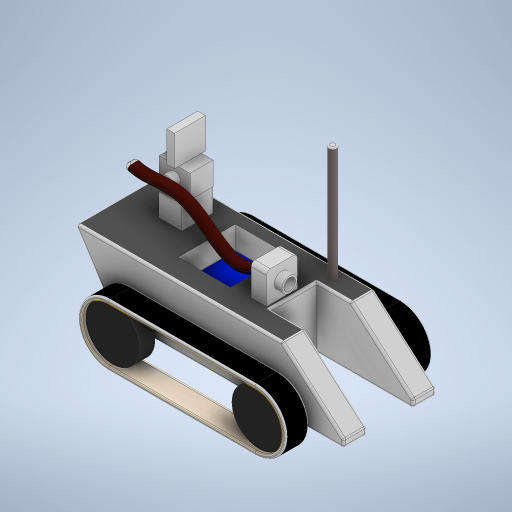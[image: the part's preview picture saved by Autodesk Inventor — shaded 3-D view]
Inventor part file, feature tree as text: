
AUTODESK INVENTOR PART (.ipt)
format: ipt  version: 2023.1 (Build 271208000, 208)  size: 786,944 bytes
history: native  units: in
note: dims shown in document units (in); Inventor stores cm internally (conversion verified against a paired STEP export)
features: sketch x21, extrude x19, fillet x7, plane x2, other x2, thicken_offset x1, mirror x1, sweep x1
ambient origin geometry x8: Origin, YZ Plane, XZ Plane, XY Plane, X Axis, Y Axis, Z Axis, Center Point
bodies: Solid1 (feature_tree)
feature tree (54):
  extrude  "Extrusion1"  Depth=2.7559in
  thicken_offset  "Thicken1"
  extrude  "Extrusion2"  Depth=3.7402in
  extrude  "Extrusion3"  Depth=7.4803in
  extrude  "Extrusion4"  Depth=0.1969in
  plane  "Work Plane2"
  mirror  "Mirror1"
  extrude  "Extrusion5"  Depth=0.9843in TaperAngle=0.0deg
  extrude  "Extrusion6"  Depth=0.7874in
  extrude  "Extrusion7"  Depth=0.3937in
  extrude  "Extrusion8"  Depth=0.7874in
  extrude  "Extrusion9"  Depth=1.7717in
  extrude  "Extrusion10"  Depth=1.1811in
  extrude  "Extrusion11"  Depth=1.1811in TaperAngle=0.0deg
  sketch  "Sketch13"  dims[d32=1.5748in d33=1.1811in d34=1.1811in d35=0.0in]
  extrude  "Extrusion12"  Depth=0.1969in TaperAngle=0.0deg
  plane  "Work Plane5"
  sweep  "Sweep1"
  fillet  "Fillet1"  Radius=1.1811in
  extrude  "Extrusion13"  Depth=0.3937in TaperAngle=0.0deg
  extrude  "Extrusion14"  Depth=0.3937in TaperAngle=0.0deg
  extrude  "Extrusion15"  Depth=1.5748in
  extrude  "Extrusion16"  Depth=0.7874in
  extrude  "Extrusion17"  Depth=0.7874in TaperAngle=0.0deg
  fillet  "Fillet2"  Radius=0.5906in
  fillet  "Fillet3"  [1 undecoded]
  fillet  "Fillet4"  Radius=0.0787in
  fillet  "Fillet5"  Radius=0.0394in
  fillet  "Fillet6"  Radius=0.5906in
  fillet  "Fillet7"  Radius=0.7874in
  sketch  "Sketch1"  dims[d0=2.7559in d1=2.7559in]
  sketch  "Sketch2"  dims[d2=0.7874in d3=0.0in d4=3.7402in]
  other  "Srf1"
  sketch  "Sketch3"  dims[d5=3.7402in d6=7.4803in]
  sketch  "Sketch4"  dims[d7=0.1969in d8=0.0in d9=0.1969in]
  sketch  "Sketch5"  dims[d10=0.1969in d11=0.9843in d12=0.0in]
  other  "Srf2"
  sketch  "Sketch6"  dims[d13=0.7874in d14=0.7874in]
  sketch  "Sketch7"  dims[d15=0.3937in d16=0.0in d17=13.7795in]
  sketch  "Sketch8"  dims[d18=0.7874in d19=2.3622in]
  sketch  "Sketch9"  dims[d20=2.3622in d21=0.0in d22=1.7717in]
  sketch  "Sketch10"  dims[d23=1.1811in d24=0.0in d25=1.1811in]
  sketch  "Sketch11"  dims[d26=1.5748in d27=1.1811in d28=0.0in]
  sketch  "Sketch12"  dims[d29=0.5906in d30=0.1969in d31=0.0in]
  sketch  "Sketch14"  dims[d36=0.5906in d37=0.3937in d38=0.0in]
  sketch  "Sketch15"  dims[d39=0.3937in d40=5.9055in d41=0.0in]
  sketch  "Sketch16"  dims[d42=0.7874in d43=1.5748in]
  sketch  "Sketch17"  dims[d44=1.5748in d45=0.0in d46=0.7874in]
  sketch  "Sketch18"  dims[d47=0.3937in d48=1.1811in d49=0.0in d50=0.0in d51=0.0394in d52=0.0in d53=0.5906in d54=0.0in d55=0.0in d56=0.0787in d57=0.0394in d58=0.0in d59=0.5906in d60=0.7874in d61=0.0in]
  sketch  "Sketch19"  dims[d62=0.3937in d63=1.5748in]
  sketch  "Sketch20"  dims[d64=1.5748in d65=0.0in d66=0.3937in]
  sketch  "Sketch21"  dims[d67=0.7874in d68=0.1969in d69=0.0in d70=1.1811in d71=0.0in d72=0.1181in d73=0.1969in d74=0.1969in d75=0.0787in d76=0.0787in d77=0.0787in]
  extrude  "ExtrusionSrf1"  Depth=1.5748in
  extrude  "ExtrusionSrf2"  Depth=0.3937in
note: 1 required parameter value undecoded (feature->parameter linkage not recoverable at this tier; creation-order binding heuristic only, values carry confidence <= 0.55)
